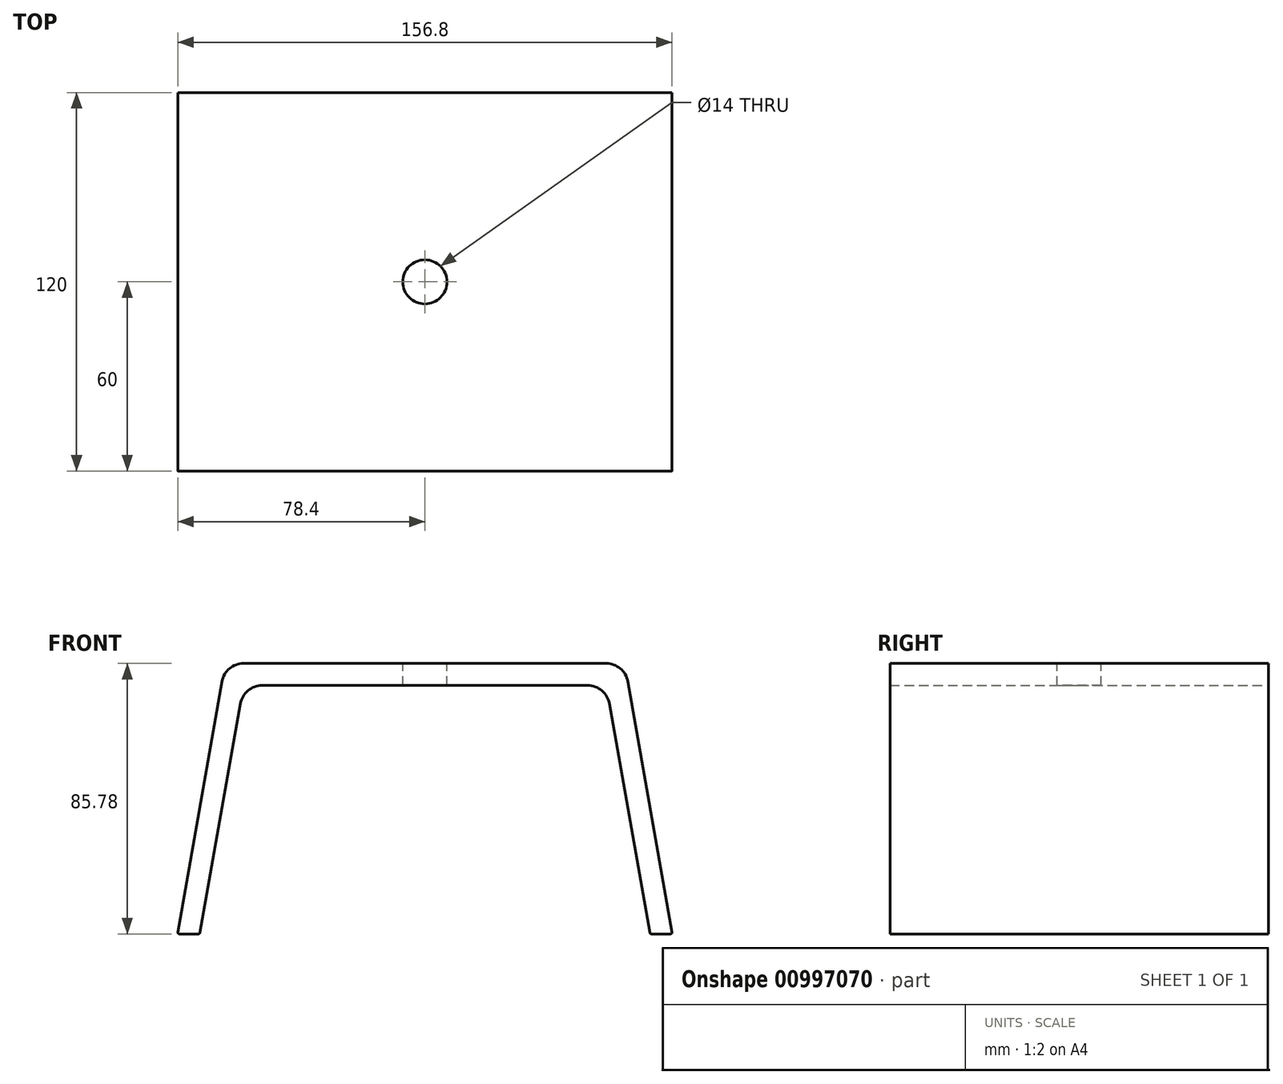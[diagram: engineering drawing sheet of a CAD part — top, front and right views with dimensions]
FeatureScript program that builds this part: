
annotation { "Feature Type Name" : "Feature", "Feature Type Description" : "" }
export const myFeature = defineFeature(function(context is Context, id is Id, definition is map)
    precondition{}
    {
        {
            var Q0;
            Q0=qCreatedBy(makeId("Front.planeOp"),FACE);
            var sketch = newSketch(context, id + "F0", { "sketchPlane" : qUnion([Q0])});
            skLineSegment(sketch, "E0", {"start": v(-71.32, 0.41) * mm, "end": v(-58.52, 73) * mm});
            skLineSegment(sketch, "E1", {"start": v(-51.63, 78.78) * mm, "end": v(51.63, 78.78) * mm});
            skLineSegment(sketch, "E2", {"start": v(58.52, 73) * mm, "end": v(71.32, 0.41) * mm});
            skPoint(sketch, "E3", {"position": v(0, 78.78) * mm});
            skLineSegment(sketch, "E4.0", {"start": v(64.4, 80) * mm, "end": v(78.4, 0.59) * mm});
            skLineSegment(sketch, "E4.1", {"start": v(-57.5, 85.78) * mm, "end": v(57.5, 85.78) * mm});
            skLineSegment(sketch, "E4.2", {"start": v(-78.4, 0.59) * mm, "end": v(-64.4, 80) * mm});
            skLineSegment(sketch, "E5", {"start": v(-77.9, 0) * mm, "end": v(-71.81, 0) * mm});
            skLineSegment(sketch, "E6", {"start": v(71.81, 0) * mm, "end": v(77.9, 0) * mm});
            skPoint(sketch, "E7.visualSharp", {"position": v(-57.5, 78.78) * mm});
            skArc(sketch, "E7.filletArc", {"start": v(-51.63, 78.78) * mm, "mid": v(-56.13, 77.15) * mm, "end": v(-58.52, 73) * mm});
            skPoint(sketch, "E8.visualSharp", {"position": v(57.5, 78.78) * mm});
            skArc(sketch, "E8.filletArc", {"start": v(58.52, 73) * mm, "mid": v(56.13, 77.15) * mm, "end": v(51.63, 78.78) * mm});
            skPoint(sketch, "E9.visualSharp", {"position": v(-63.37, 85.78) * mm});
            skArc(sketch, "E9.filletArc", {"start": v(-57.5, 85.78) * mm, "mid": v(-62, 84.15) * mm, "end": v(-64.4, 80) * mm});
            skPoint(sketch, "E10.visualSharp", {"position": v(63.37, 85.78) * mm});
            skArc(sketch, "E10.filletArc", {"start": v(64.4, 80) * mm, "mid": v(62, 84.15) * mm, "end": v(57.5, 85.78) * mm});
            skPoint(sketch, "E11.visualSharp", {"position": v(-78.5, 0) * mm});
            skArc(sketch, "E11.filletArc", {"start": v(-78.4, 0.59) * mm, "mid": v(-78.29, 0.18) * mm, "end": v(-77.9, 0) * mm});
            skPoint(sketch, "E12.visualSharp", {"position": v(-71.4, 0) * mm});
            skArc(sketch, "E12.filletArc", {"start": v(-71.81, 0) * mm, "mid": v(-71.5, 0.12) * mm, "end": v(-71.32, 0.41) * mm});
            skPoint(sketch, "E13.visualSharp", {"position": v(71.4, 0) * mm});
            skArc(sketch, "E13.filletArc", {"start": v(71.32, 0.41) * mm, "mid": v(71.5, 0.12) * mm, "end": v(71.81, 0) * mm});
            skPoint(sketch, "E14.visualSharp", {"position": v(78.5, 0) * mm});
            skArc(sketch, "E14.filletArc", {"start": v(77.9, 0) * mm, "mid": v(78.29, 0.18) * mm, "end": v(78.4, 0.59) * mm});
            skSolve(sketch);
        }
        {
            var Q0;
            Q0 = qSketchRegion(id + "F0", true);
            extrude(context, id + "F1", {"entities" : qUnion([Q0]), "depth" : 120 * mm, "offsetDistance" : 25 * mm});
        }
        {
            var Q0;
            Q0=makeQuery(id+"F1.opExtrude","SWEPT_FACE",FACE,{"disambiguationData":[OSD([sQuery(id+"F0.wireOp",EDGE,"E4.1")])]});
            var sketch = newSketch(context, id + "F2", { "sketchPlane" : qUnion([Q0])});
            skCircle(sketch, "E15", {"center": v(0, -60) * mm, "radius": 7 * mm});
            skSolve(sketch);
        }
        {
            var Q0;
            Q0 = qSketchRegion(id + "F2", true);
            extrude(context, id + "F3", {"entities" : qUnion([Q0]), "operationType" : NewBodyOperationType.REMOVE, "oppositeDirection" : true, "depth" : 25 * mm, "offsetDistance" : 25 * mm});
        }
    });
